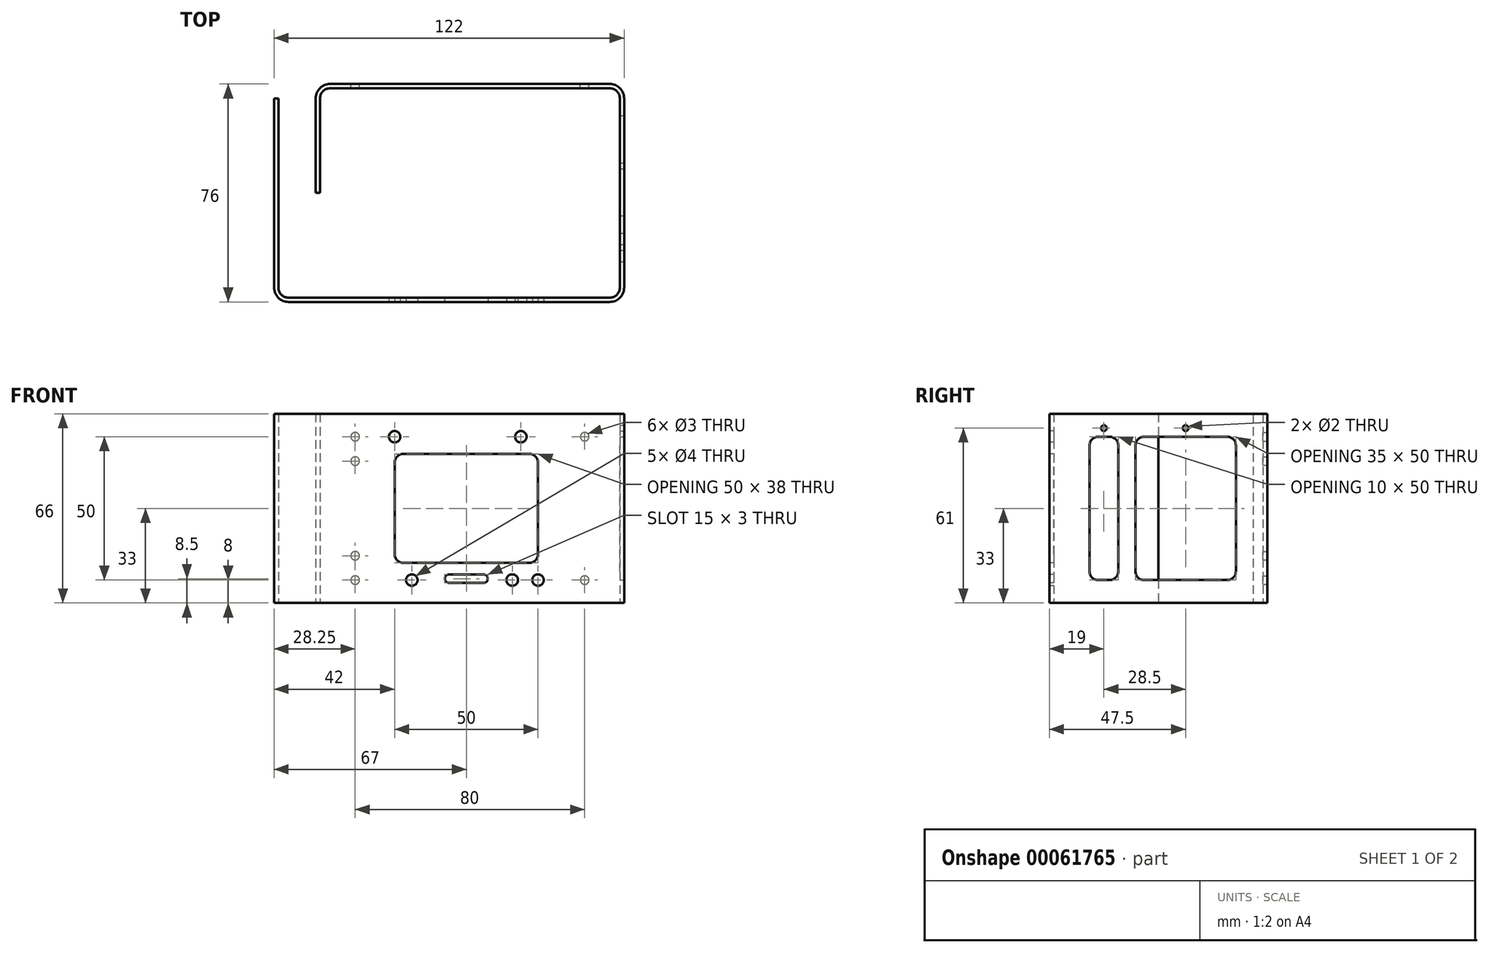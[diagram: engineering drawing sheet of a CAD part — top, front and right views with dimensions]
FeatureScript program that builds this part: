
annotation { "Feature Type Name" : "Feature", "Feature Type Description" : "" }
export const myFeature = defineFeature(function(context is Context, id is Id, definition is map)
    precondition{}
    {
        {
            var Q0;
            Q0=qCreatedBy(makeId("Top.planeOp"),FACE);
            var sketch = newSketch(context, id + "F0", { "sketchPlane" : qUnion([Q0])});
            skLineSegment(sketch, "E0", {"start": v(-66.75, 33) * mm, "end": v(-66.75, -33) * mm});
            skLineSegment(sketch, "E1", {"start": v(-63.25, -36.5) * mm, "end": v(48.75, -36.5) * mm});
            skLineSegment(sketch, "E2", {"start": v(52.25, -33) * mm, "end": v(52.25, 33) * mm});
            skLineSegment(sketch, "E3", {"start": v(48.75, 36.5) * mm, "end": v(-48.75, 36.5) * mm});
            skLineSegment(sketch, "E4", {"start": v(-52.25, 33) * mm, "end": v(-52.25, 0) * mm});
            skLineSegment(sketch, "E5.0", {"start": v(-53.75, 33) * mm, "end": v(-53.75, 0) * mm});
            skLineSegment(sketch, "E5.1", {"start": v(-68.25, 33) * mm, "end": v(-68.25, -33) * mm});
            skLineSegment(sketch, "E5.2", {"start": v(-63.25, -38) * mm, "end": v(48.75, -38) * mm});
            skLineSegment(sketch, "E5.3", {"start": v(53.75, -33) * mm, "end": v(53.75, 33) * mm});
            skLineSegment(sketch, "E5.4", {"start": v(48.75, 38) * mm, "end": v(-48.75, 38) * mm});
            skLineSegment(sketch, "E6", {"start": v(-52.25, 0) * mm, "end": v(-53.75, 0) * mm});
            skLineSegment(sketch, "E7", {"start": v(-66.75, 33) * mm, "end": v(-68.25, 33) * mm});
            skPoint(sketch, "E8.visualSharp", {"position": v(-66.75, -36.5) * mm});
            skArc(sketch, "E8.filletArc", {"start": v(-66.75, -33) * mm, "mid": v(-65.72, -35.47) * mm, "end": v(-63.25, -36.5) * mm});
            skPoint(sketch, "E9.visualSharp", {"position": v(52.25, -36.5) * mm});
            skArc(sketch, "E9.filletArc", {"start": v(48.75, -36.5) * mm, "mid": v(51.22, -35.47) * mm, "end": v(52.25, -33) * mm});
            skPoint(sketch, "E10.visualSharp", {"position": v(52.25, 36.5) * mm});
            skArc(sketch, "E10.filletArc", {"start": v(52.25, 33) * mm, "mid": v(51.22, 35.47) * mm, "end": v(48.75, 36.5) * mm});
            skPoint(sketch, "E11.visualSharp", {"position": v(-52.25, 36.5) * mm});
            skArc(sketch, "E11.filletArc", {"start": v(-48.75, 36.5) * mm, "mid": v(-51.22, 35.47) * mm, "end": v(-52.25, 33) * mm});
            skPoint(sketch, "E12.visualSharp", {"position": v(-68.25, -38) * mm});
            skArc(sketch, "E12.filletArc", {"start": v(-68.25, -33) * mm, "mid": v(-66.79, -36.54) * mm, "end": v(-63.25, -38) * mm});
            skPoint(sketch, "E13.visualSharp", {"position": v(53.75, -38) * mm});
            skArc(sketch, "E13.filletArc", {"start": v(48.75, -38) * mm, "mid": v(52.29, -36.54) * mm, "end": v(53.75, -33) * mm});
            skPoint(sketch, "E14.visualSharp", {"position": v(53.75, 38) * mm});
            skArc(sketch, "E14.filletArc", {"start": v(53.75, 33) * mm, "mid": v(52.29, 36.54) * mm, "end": v(48.75, 38) * mm});
            skPoint(sketch, "E15.visualSharp", {"position": v(-53.75, 38) * mm});
            skArc(sketch, "E15.filletArc", {"start": v(-48.75, 38) * mm, "mid": v(-52.29, 36.54) * mm, "end": v(-53.75, 33) * mm});
            skLineSegment(sketch, "E16", {"start": v(52.25, 0) * mm, "end": v(-12.48, 0) * mm, "construction": true});
            skLineSegment(sketch, "E17", {"start": v(0, 36.5) * mm, "end": v(0, -15.26) * mm, "construction": true});
            skSolve(sketch);
        }
        {
            var Q0;
            Q0 = qSketchRegion(id + "F0", true);
            extrude(context, id + "F1", {"entities" : qUnion([Q0]), "depth" : 66 * mm});
        }
        {
            var Q0;
            Q0=makeQuery(id+"F1.opExtrude","SWEPT_FACE",FACE,{"disambiguationData":[OSD([sQuery(id+"F0.wireOp",EDGE,"E5.2")])]});
            var sketch = newSketch(context, id + "F2", { "sketchPlane" : qUnion([Q0])});
            skLineSegment(sketch, "E18.bottom", {"start": v(-23.25, 52) * mm, "end": v(20.75, 52) * mm});
            skLineSegment(sketch, "E18.top", {"start": v(-23.25, 14) * mm, "end": v(20.75, 14) * mm});
            skLineSegment(sketch, "E18.left", {"start": v(-26.25, 49) * mm, "end": v(-26.25, 17) * mm});
            skLineSegment(sketch, "E18.right", {"start": v(23.75, 49) * mm, "end": v(23.75, 17) * mm});
            skLineSegment(sketch, "E19", {"start": v(-63.25, 33) * mm, "end": v(43.75, 33) * mm, "construction": true});
            skLineSegment(sketch, "E20", {"start": v(23.75, 33) * mm, "end": v(-26.25, 33) * mm, "construction": true});
            skLineSegment(sketch, "E21", {"start": v(-1.25, 52) * mm, "end": v(-1.25, 14) * mm, "construction": true});
            skLineSegment(sketch, "E22", {"start": v(-7.25, 66) * mm, "end": v(-7.25, 0) * mm, "construction": true});
            skPoint(sketch, "E23.visualSharp", {"position": v(-26.25, 52) * mm});
            skArc(sketch, "E23.filletArc", {"start": v(-23.25, 52) * mm, "mid": v(-25.37, 51.12) * mm, "end": v(-26.25, 49) * mm});
            skPoint(sketch, "E24.visualSharp", {"position": v(23.75, 52) * mm});
            skArc(sketch, "E24.filletArc", {"start": v(23.75, 49) * mm, "mid": v(22.87, 51.12) * mm, "end": v(20.75, 52) * mm});
            skPoint(sketch, "E25.visualSharp", {"position": v(23.75, 14) * mm});
            skArc(sketch, "E25.filletArc", {"start": v(20.75, 14) * mm, "mid": v(22.87, 14.88) * mm, "end": v(23.75, 17) * mm});
            skPoint(sketch, "E26.visualSharp", {"position": v(-26.25, 14) * mm});
            skArc(sketch, "E26.filletArc", {"start": v(-26.25, 17) * mm, "mid": v(-25.37, 14.88) * mm, "end": v(-23.25, 14) * mm});
            skCircle(sketch, "E27", {"center": v(-30.25, 33) * mm, "radius": 1.5 * mm});
            skCircle(sketch, "E28.MirrorC", {"center": v(27.75, 33) * mm, "radius": 1.5 * mm});
            skCircle(sketch, "E29", {"center": v(-26.25, 58) * mm, "radius": 2 * mm});
            skCircle(sketch, "E30.MirrorC", {"center": v(23.75, 58) * mm, "radius": 2 * mm});
            skCircle(sketch, "E31.MirrorC", {"center": v(-26.25, 8) * mm, "radius": 2 * mm});
            skCircle(sketch, "E32.MirrorC", {"center": v(23.75, 8) * mm, "radius": 2 * mm});
            skLineSegment(sketch, "E33.bottom", {"start": v(-7.25, 7) * mm, "end": v(4.75, 7) * mm});
            skPoint(sketch, "E34.visualSharp", {"position": v(6.25, 10) * mm});
            skLineSegment(sketch, "E33.top", {"start": v(-7.25, 10) * mm, "end": v(4.75, 10) * mm});
            skArc(sketch, "E35.filletArc", {"start": v(-7.25, 10) * mm, "mid": v(-8.31, 9.56) * mm, "end": v(-8.75, 8.5) * mm});
            skLineSegment(sketch, "E33.left", {"start": v(-8.75, 8.5) * mm, "end": v(-8.75, 8.5) * mm});
            skLineSegment(sketch, "E33.right", {"start": v(6.25, 8.5) * mm, "end": v(6.25, 8.5) * mm});
            skArc(sketch, "E36.filletArc", {"start": v(-8.75, 8.5) * mm, "mid": v(-8.31, 7.44) * mm, "end": v(-7.25, 7) * mm});
            skArc(sketch, "E37.filletArc", {"start": v(4.75, 7) * mm, "mid": v(5.81, 7.44) * mm, "end": v(6.25, 8.5) * mm});
            skArc(sketch, "E34.filletArc", {"start": v(6.25, 8.5) * mm, "mid": v(5.81, 9.56) * mm, "end": v(4.75, 10) * mm});
            skCircle(sketch, "E38", {"center": v(-11.75, 8.5) * mm, "radius": 0.75 * mm});
            skPoint(sketch, "E39", {"position": v(-1.25, 10) * mm});
            skLineSegment(sketch, "E40", {"start": v(-11.75, 8.5) * mm, "end": v(6.89, 8.5) * mm, "construction": true});
            skPoint(sketch, "E35.visualSharp", {"position": v(-8.75, 10) * mm});
            skPoint(sketch, "E36.visualSharp", {"position": v(-8.75, 7) * mm});
            skPoint(sketch, "E37.visualSharp", {"position": v(6.25, 7) * mm});
            skLineSegment(sketch, "E41", {"start": v(-1.25, 10) * mm, "end": v(-1.25, 7) * mm, "construction": true});
            skCircle(sketch, "E42.MirrorC", {"center": v(9.25, 8.5) * mm, "radius": 0.75 * mm});
            skLineSegment(sketch, "E43", {"start": v(-26.25, 8) * mm, "end": v(-26.25, 58) * mm, "construction": true});
            skLineSegment(sketch, "E44", {"start": v(23.75, 58) * mm, "end": v(23.75, 8) * mm, "construction": true});
            skLineSegment(sketch, "E45", {"start": v(-26.25, 8) * mm, "end": v(23.75, 8) * mm, "construction": true});
            skLineSegment(sketch, "E46", {"start": v(23.75, 58) * mm, "end": v(-26.25, 58) * mm, "construction": true});
            skCircle(sketch, "E47", {"center": v(-20.25, 8) * mm, "radius": 2 * mm});
            skCircle(sketch, "E48.MirrorC", {"center": v(-20.25, 58) * mm, "radius": 2 * mm});
            skCircle(sketch, "E49.MirrorC", {"center": v(17.75, 58) * mm, "radius": 2 * mm});
            skCircle(sketch, "E50", {"center": v(14.75, 8) * mm, "radius": 2 * mm});
            skPoint(sketch, "E51", {"position": v(-63.25, 33) * mm});
            skSolve(sketch);
        }
        {
            var Q0;
            Q0=makeQuery(id+"F2.imprint","IMPRINT",FACE,{"disambiguationData":[TD([[makeQuery(id+"F2.imprint","IMPRINT",EDGE,{"derivedFrom":sQuery(id+"F2.wireOp",EDGE,"E18.bottom")}),-1.0]])]});
            var Q1;
            Q1=makeQuery(id+"F2.imprint","IMPRINT",FACE,{"disambiguationData":[TD([[makeQuery(id+"F2.imprint","IMPRINT",EDGE,{"derivedFrom":sQuery(id+"F2.wireOp",EDGE,"5223969e-9384-4705-a09f-08a9d0864926")}),1.0]])]});
            var Q2;
            Q2=makeQuery(id+"F2.imprint","IMPRINT",FACE,{"disambiguationData":[TD([[makeQuery(id+"F2.imprint","IMPRINT",EDGE,{"derivedFrom":sQuery(id+"F2.wireOp",EDGE,"b6238159-0034-45e9-8c88-9dabcd8353630.MirrorC")}),-1.0]])]});
            var Q3;
            Q3=makeQuery(id+"F2.imprint","IMPRINT",FACE,{"disambiguationData":[TD([[makeQuery(id+"F2.imprint","IMPRINT",EDGE,{"derivedFrom":sQuery(id+"F2.wireOp",EDGE,"E29")}),1.0]])]});
            var Q4;
            Q4=makeQuery(id+"F2.imprint","IMPRINT",FACE,{"disambiguationData":[TD([[makeQuery(id+"F2.imprint","IMPRINT",EDGE,{"derivedFrom":sQuery(id+"F2.wireOp",EDGE,"E30.MirrorC")}),-1.0]])]});
            var Q5;
            Q5=makeQuery(id+"F2.imprint","IMPRINT",FACE,{"disambiguationData":[TD([[makeQuery(id+"F2.imprint","IMPRINT",EDGE,{"derivedFrom":sQuery(id+"F2.wireOp",EDGE,"E32.MirrorC")}),1.0]])]});
            var Q6;
            Q6=makeQuery(id+"F2.imprint","IMPRINT",FACE,{"disambiguationData":[TD([[makeQuery(id+"F2.imprint","IMPRINT",EDGE,{"derivedFrom":sQuery(id+"F2.wireOp",EDGE,"E31.MirrorC")}),-1.0]])]});
            var Q7;
            Q7=makeQuery(id+"F2.imprint","IMPRINT",FACE,{"disambiguationData":[TD([[makeQuery(id+"F2.imprint","IMPRINT",EDGE,{"derivedFrom":sQuery(id+"F2.wireOp",EDGE,"E33.bottom")}),1.0]])]});
            var Q8;
            Q8=makeQuery(id+"F2.imprint","IMPRINT",FACE,{"disambiguationData":[TD([[makeQuery(id+"F2.imprint","IMPRINT",EDGE,{"derivedFrom":sQuery(id+"F2.wireOp",EDGE,"E47")}),1.0]])]});
            var Q9;
            Q9=makeQuery(id+"F2.imprint","IMPRINT",FACE,{"disambiguationData":[TD([[makeQuery(id+"F2.imprint","IMPRINT",EDGE,{"derivedFrom":sQuery(id+"F2.wireOp",EDGE,"E48.MirrorC")}),-1.0]])]});
            var Q10;
            Q10=makeQuery(id+"F2.imprint","IMPRINT",FACE,{"disambiguationData":[TD([[makeQuery(id+"F2.imprint","IMPRINT",EDGE,{"derivedFrom":sQuery(id+"F2.wireOp",EDGE,"E49.MirrorC")}),1.0]])]});
            var Q11;
            Q11=makeQuery(id+"F2.imprint","IMPRINT",FACE,{"disambiguationData":[TD([[makeQuery(id+"F2.imprint","IMPRINT",EDGE,{"derivedFrom":sQuery(id+"F2.wireOp",EDGE,"E50")}),1.0]])]});
            extrude(context, id + "F3", {"entities" : qUnion([Q0, Q1, Q2, Q3, Q4, Q5, Q6, Q7, Q8, Q9, Q10, Q11]), "operationType" : NewBodyOperationType.REMOVE, "oppositeDirection" : true, "depth" : 25 * mm});
        }
        {
            var Q0;
            Q0=makeQuery(id+"F1.opExtrude","SWEPT_FACE",FACE,{"disambiguationData":[OSD([sQuery(id+"F0.wireOp",EDGE,"E5.4")])]});
            var sketch = newSketch(context, id + "F4", { "sketchPlane" : qUnion([Q0])});
            skCircle(sketch, "E52", {"center": v(-40, 58) * mm, "radius": 1.5 * mm});
            skLineSegment(sketch, "E53", {"start": v(-40, 58) * mm, "end": v(-40, 8) * mm, "construction": true});
            skLineSegment(sketch, "E54", {"start": v(-40, 8) * mm, "end": v(40, 8) * mm, "construction": true});
            skLineSegment(sketch, "E55", {"start": v(40, 8) * mm, "end": v(40, 58) * mm, "construction": true});
            skLineSegment(sketch, "E56", {"start": v(40, 58) * mm, "end": v(-40, 58) * mm, "construction": true});
            skCircle(sketch, "E57", {"center": v(-40, 8) * mm, "radius": 1.5 * mm});
            skCircle(sketch, "E58", {"center": v(40, 8) * mm, "radius": 1.5 * mm});
            skCircle(sketch, "E59", {"center": v(40, 58) * mm, "radius": 1.5 * mm});
            skLineSegment(sketch, "E60", {"start": v(0, 0) * mm, "end": v(0, 116) * mm, "construction": true});
            skPoint(sketch, "E60.endSnap0", {"position": v(0, 0) * mm});
            skPoint(sketch, "E61", {"position": v(0, 58) * mm});
            skCircle(sketch, "E62", {"center": v(40, 49.5) * mm, "radius": 1.5 * mm});
            skCircle(sketch, "E63", {"center": v(40, 16.5) * mm, "radius": 1.5 * mm});
            skLineSegment(sketch, "E64", {"start": v(33.75, 66) * mm, "end": v(33.75, 0) * mm, "construction": true});
            skLineSegment(sketch, "E65", {"start": v(33.75, 33) * mm, "end": v(24.95, 33) * mm, "construction": true});
            skLineSegment(sketch, "E66", {"start": v(29.35, 33) * mm, "end": v(29.35, 66) * mm, "construction": true});
            skLineSegment(sketch, "E67", {"start": v(29.35, 33) * mm, "end": v(29.35, 0) * mm, "construction": true});
            skLineSegment(sketch, "E68", {"start": v(29.35, 16.5) * mm, "end": v(44.25, 16.5) * mm, "construction": true});
            skLineSegment(sketch, "E69", {"start": v(29.35, 49.5) * mm, "end": v(45.75, 49.5) * mm, "construction": true});
            skSolve(sketch);
        }
        {
            var Q0;
            Q0=makeQuery(id+"F4.imprint","IMPRINT",FACE,{"disambiguationData":[TD([[makeQuery(id+"F4.imprint","IMPRINT",EDGE,{"derivedFrom":sQuery(id+"F4.wireOp",EDGE,"E52")}),1.0]])]});
            var Q1;
            Q1=makeQuery(id+"F4.imprint","IMPRINT",FACE,{"disambiguationData":[TD([[makeQuery(id+"F4.imprint","IMPRINT",EDGE,{"derivedFrom":sQuery(id+"F4.wireOp",EDGE,"E57")}),1.0]])]});
            var Q2;
            Q2=makeQuery(id+"F4.imprint","IMPRINT",FACE,{"disambiguationData":[TD([[makeQuery(id+"F4.imprint","IMPRINT",EDGE,{"derivedFrom":sQuery(id+"F4.wireOp",EDGE,"E58")}),1.0]])]});
            var Q3;
            Q3=makeQuery(id+"F4.imprint","IMPRINT",FACE,{"disambiguationData":[TD([[makeQuery(id+"F4.imprint","IMPRINT",EDGE,{"derivedFrom":sQuery(id+"F4.wireOp",EDGE,"E59")}),1.0]])]});
            var Q4;
            Q4=makeQuery(id+"F4.imprint","IMPRINT",FACE,{"disambiguationData":[TD([[makeQuery(id+"F4.imprint","IMPRINT",EDGE,{"derivedFrom":sQuery(id+"F4.wireOp",EDGE,"E63")}),1.0]])]});
            var Q5;
            Q5=makeQuery(id+"F4.imprint","IMPRINT",FACE,{"disambiguationData":[TD([[makeQuery(id+"F4.imprint","IMPRINT",EDGE,{"derivedFrom":sQuery(id+"F4.wireOp",EDGE,"E62")}),1.0]])]});
            extrude(context, id + "F5", {"entities" : qUnion([Q0, Q1, Q2, Q3, Q4, Q5]), "operationType" : NewBodyOperationType.REMOVE, "oppositeDirection" : true, "depth" : 25 * mm});
        }
        {
            var Q0;
            Q0=makeQuery(id+"F1.opExtrude","SWEPT_FACE",FACE,{"disambiguationData":[OSD([sQuery(id+"F0.wireOp",EDGE,"E5.3")])]});
            var sketch = newSketch(context, id + "F6", { "sketchPlane" : qUnion([Q0])});
            skLineSegment(sketch, "E70.bottom", {"start": v(-21, 58) * mm, "end": v(-17, 58) * mm});
            skLineSegment(sketch, "E70.top", {"start": v(-21, 8) * mm, "end": v(-17, 8) * mm});
            skLineSegment(sketch, "E70.left", {"start": v(-24, 55) * mm, "end": v(-24, 11) * mm});
            skLineSegment(sketch, "E70.right", {"start": v(-14, 55) * mm, "end": v(-14, 11) * mm});
            skLineSegment(sketch, "E71.bottom", {"start": v(-5, 58) * mm, "end": v(24, 58) * mm});
            skLineSegment(sketch, "E71.top", {"start": v(-5, 8) * mm, "end": v(24, 8) * mm});
            skLineSegment(sketch, "E71.left", {"start": v(-8, 55) * mm, "end": v(-8, 11) * mm});
            skLineSegment(sketch, "E71.right", {"start": v(27, 55) * mm, "end": v(27, 11) * mm});
            skLineSegment(sketch, "E72", {"start": v(-14, 58) * mm, "end": v(-8, 58) * mm, "construction": true});
            skLineSegment(sketch, "E73", {"start": v(-14, 8) * mm, "end": v(-8, 8) * mm, "construction": true});
            skPoint(sketch, "E74.visualSharp", {"position": v(-24, 58) * mm});
            skArc(sketch, "E74.filletArc", {"start": v(-21, 58) * mm, "mid": v(-23.12, 57.12) * mm, "end": v(-24, 55) * mm});
            skPoint(sketch, "E75.visualSharp", {"position": v(-14, 58) * mm});
            skArc(sketch, "E75.filletArc", {"start": v(-14, 55) * mm, "mid": v(-14.88, 57.12) * mm, "end": v(-17, 58) * mm});
            skPoint(sketch, "E76.visualSharp", {"position": v(-24, 8) * mm});
            skArc(sketch, "E76.filletArc", {"start": v(-24, 11) * mm, "mid": v(-23.12, 8.88) * mm, "end": v(-21, 8) * mm});
            skPoint(sketch, "E77.visualSharp", {"position": v(-14, 8) * mm});
            skArc(sketch, "E77.filletArc", {"start": v(-17, 8) * mm, "mid": v(-14.88, 8.88) * mm, "end": v(-14, 11) * mm});
            skPoint(sketch, "E78.visualSharp", {"position": v(-8, 8) * mm});
            skArc(sketch, "E78.filletArc", {"start": v(-8, 11) * mm, "mid": v(-7.12, 8.88) * mm, "end": v(-5, 8) * mm});
            skPoint(sketch, "E79.visualSharp", {"position": v(27, 8) * mm});
            skArc(sketch, "E79.filletArc", {"start": v(24, 8) * mm, "mid": v(26.12, 8.88) * mm, "end": v(27, 11) * mm});
            skPoint(sketch, "E80.visualSharp", {"position": v(27, 58) * mm});
            skArc(sketch, "E80.filletArc", {"start": v(27, 55) * mm, "mid": v(26.12, 57.12) * mm, "end": v(24, 58) * mm});
            skPoint(sketch, "E81.visualSharp", {"position": v(-8, 58) * mm});
            skArc(sketch, "E81.filletArc", {"start": v(-5, 58) * mm, "mid": v(-7.12, 57.12) * mm, "end": v(-8, 55) * mm});
            skCircle(sketch, "E82", {"center": v(-19, 61) * mm, "radius": 1 * mm});
            skLineSegment(sketch, "E83", {"start": v(-24, 33) * mm, "end": v(27, 33) * mm, "construction": true});
            skLineSegment(sketch, "E84", {"start": v(-19, 58) * mm, "end": v(-19, 8) * mm, "construction": true});
            skPoint(sketch, "E84.endSnap0", {"position": v(-19, 8) * mm});
            skLineSegment(sketch, "E85", {"start": v(9.5, 8) * mm, "end": v(9.5, 58) * mm, "construction": true});
            skCircle(sketch, "E86", {"center": v(9.5, 61) * mm, "radius": 1 * mm});
            skCircle(sketch, "E87.MirrorC", {"center": v(-19, 5) * mm, "radius": 1 * mm});
            skCircle(sketch, "E88.MirrorC", {"center": v(9.5, 5) * mm, "radius": 1 * mm});
            skSolve(sketch);
        }
        {
            var Q0;
            Q0=makeQuery(id+"F6.imprint","IMPRINT",FACE,{"disambiguationData":[TD([[makeQuery(id+"F6.imprint","IMPRINT",EDGE,{"derivedFrom":sQuery(id+"F6.wireOp",EDGE,"E70.bottom")}),-1.0]])]});
            var Q1;
            Q1=makeQuery(id+"F6.imprint","IMPRINT",FACE,{"disambiguationData":[TD([[makeQuery(id+"F6.imprint","IMPRINT",EDGE,{"derivedFrom":sQuery(id+"F6.wireOp",EDGE,"E71.bottom")}),-1.0]])]});
            var Q2;
            Q2=makeQuery(id+"F6.imprint","IMPRINT",FACE,{"disambiguationData":[TD([[makeQuery(id+"F6.imprint","IMPRINT",EDGE,{"derivedFrom":sQuery(id+"F6.wireOp",EDGE,"E70.bottom")}),-1.0]])]});
            var Q3;
            Q3=makeQuery(id+"F6.imprint","IMPRINT",FACE,{"disambiguationData":[TD([[makeQuery(id+"F6.imprint","IMPRINT",EDGE,{"derivedFrom":sQuery(id+"F6.wireOp",EDGE,"E71.bottom")}),-1.0]])]});
            var Q4;
            Q4=makeQuery(id+"F6.imprint","IMPRINT",FACE,{"disambiguationData":[TD([[makeQuery(id+"F6.imprint","IMPRINT",EDGE,{"derivedFrom":sQuery(id+"F6.wireOp",EDGE,"E82")}),1.0]])]});
            var Q5;
            Q5=makeQuery(id+"F6.imprint","IMPRINT",FACE,{"disambiguationData":[TD([[makeQuery(id+"F6.imprint","IMPRINT",EDGE,{"derivedFrom":sQuery(id+"F6.wireOp",EDGE,"E86")}),1.0]])]});
            var Q6;
            Q6=makeQuery(id+"F6.imprint","IMPRINT",FACE,{"disambiguationData":[TD([[makeQuery(id+"F6.imprint","IMPRINT",EDGE,{"derivedFrom":sQuery(id+"F6.wireOp",EDGE,"E88.MirrorC")}),-1.0]])]});
            var Q7;
            Q7=makeQuery(id+"F6.imprint","IMPRINT",FACE,{"disambiguationData":[TD([[makeQuery(id+"F6.imprint","IMPRINT",EDGE,{"derivedFrom":sQuery(id+"F6.wireOp",EDGE,"E87.MirrorC")}),-1.0]])]});
            extrude(context, id + "F7", {"entities" : qUnion([Q0, Q1, Q2, Q3, Q4, Q5, Q6, Q7]), "operationType" : NewBodyOperationType.REMOVE, "oppositeDirection" : true, "depth" : 25 * mm});
        }
    });
